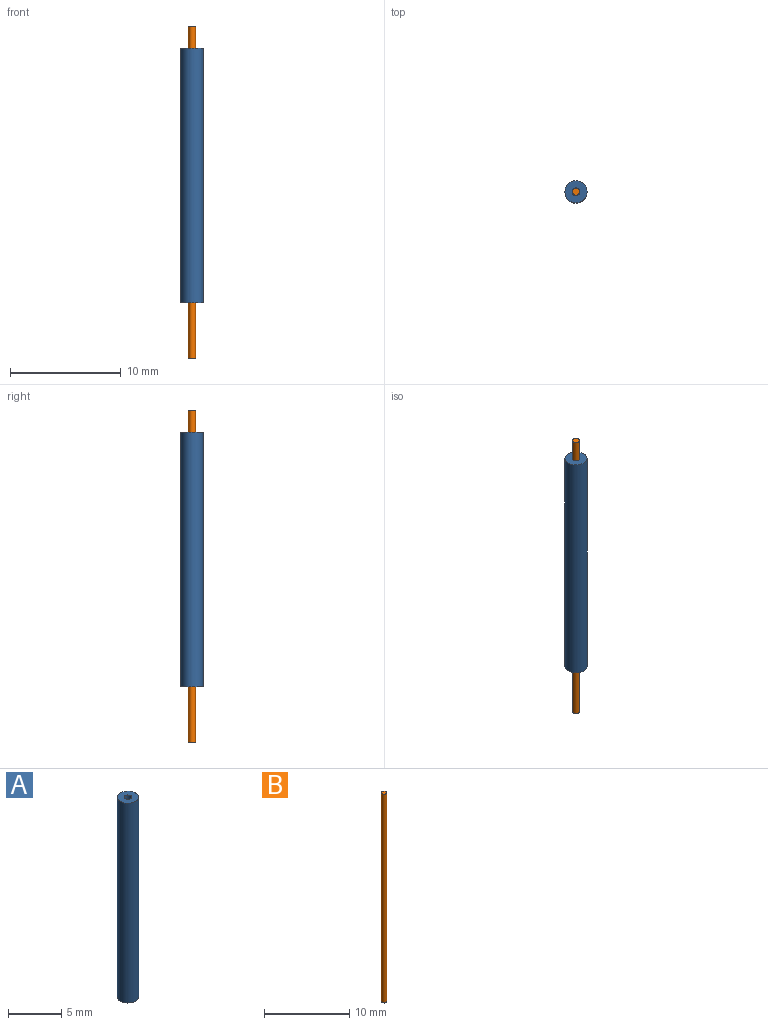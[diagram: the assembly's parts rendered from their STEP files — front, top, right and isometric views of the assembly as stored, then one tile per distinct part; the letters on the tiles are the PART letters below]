
ASSEMBLY  parts=2 mates=2
PART A: 4 faces, bbox 2x2x23 mm
  f0: cylinder r=0.35mm len=23mm, axis (0,0,-1), area 50.6mm2, adj f1,f3
  f1: plane 2x2mm, normal (0,0,1), area 2.8mm2, adj f0,f2
  f2: cylinder r=1mm len=23mm, axis (0,0,-1), area 144.5mm2, adj f1,f3
  f3: plane 2x2mm, normal (0,0,-1), area 2.8mm2, adj f0,f2
PART B: 3 faces, bbox 0.6x0.6x30 mm
  f0: plane 0.64x0.64mm, normal (0,0,-1), area 0.3mm2, adj f2
  f1: plane 0.64x0.64mm, normal (0,0,1), area 0.3mm2, adj f2
  f2: cylinder r=0.32mm len=30mm, axis (0,0,1), area 60.3mm2, adj f0,f1
PLACE A t=(-0.1,-0.02,-19.94)mm
PLACE B t=(-0.1,-0.02,-19.94)mm
MATE cylindrical A.f0 <-> B.f2  axis (0,0,-1) through (-0.1,-0.02,-14.94)mm
MATE planar B.f2 <-> A.f0  axis (0,0,1) through (-0.1,-0.02,10.06)mm
